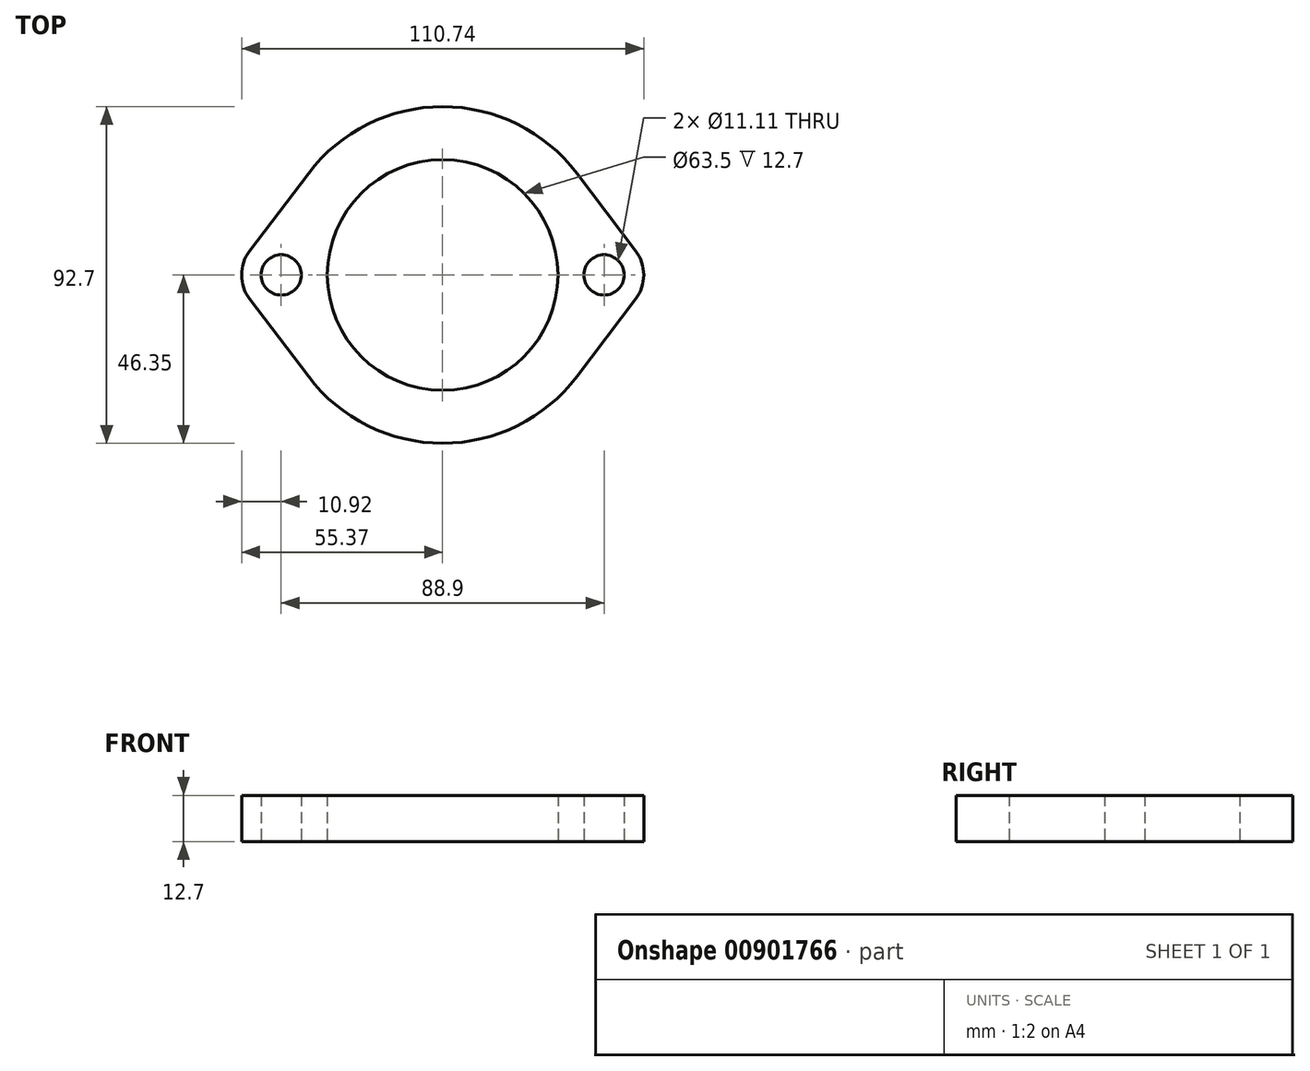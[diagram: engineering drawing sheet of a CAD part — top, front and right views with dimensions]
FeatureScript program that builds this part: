
annotation { "Feature Type Name" : "Feature", "Feature Type Description" : "" }
export const myFeature = defineFeature(function(context is Context, id is Id, definition is map)
    precondition{}
    {
        {
            var Q0;
            Q0=qCreatedBy(makeId("Top.planeOp"),FACE);
            var sketch = newSketch(context, id + "F0", { "sketchPlane" : qUnion([Q0])});
            skCircle(sketch, "E0", {"center": v(0, 0) * mm, "radius": 31.75 * mm});
            skArc(sketch, "E1", {"start": v(0, 46.35) * mm, "mid": v(-20.63, 41.51) * mm, "end": v(-36.95, 27.99) * mm});
            skCircle(sketch, "E2", {"center": v(-44.45, 0) * mm, "radius": 5.56 * mm});
            skArc(sketch, "E3", {"start": v(-53.16, 6.6) * mm, "mid": v(-54.8, 3.48) * mm, "end": v(-55.37, 0) * mm});
            skLineSegment(sketch, "E4", {"start": v(-31.75, 0) * mm, "end": v(-33.53, 0) * mm});
            skLineSegment(sketch, "E5", {"start": v(-53.16, 6.6) * mm, "end": v(-36.95, 27.99) * mm});
            skLineSegment(sketch, "E6", {"start": v(-73.33, 0) * mm, "end": v(-38.9, 0) * mm, "construction": true});
            skLineSegment(sketch, "E7", {"start": v(0, 50.51) * mm, "end": v(0, -57.19) * mm, "construction": true});
            skLineSegment(sketch, "E8.trimOffspring", {"start": v(-31.75, 0) * mm, "end": v(0, 0) * mm, "construction": true});
            skLineSegment(sketch, "E9.MirrorCS", {"start": v(-53.16, -6.6) * mm, "end": v(-36.95, -27.99) * mm});
            skArc(sketch, "E10.MirrorCS", {"start": v(-53.16, -6.6) * mm, "mid": v(-54.8, -3.48) * mm, "end": v(-55.37, 0) * mm});
            skArc(sketch, "E11.MirrorCS", {"start": v(0, -46.35) * mm, "mid": v(-20.63, -41.51) * mm, "end": v(-36.95, -27.99) * mm});
            skArc(sketch, "E12.MirrorCS", {"start": v(0, 46.35) * mm, "mid": v(20.63, 41.51) * mm, "end": v(36.95, 27.99) * mm});
            skLineSegment(sketch, "E13.MirrorCS", {"start": v(53.16, 6.6) * mm, "end": v(36.95, 27.99) * mm});
            skArc(sketch, "E14.MirrorCS", {"start": v(53.16, 6.6) * mm, "mid": v(54.8, 3.48) * mm, "end": v(55.37, 0) * mm});
            skArc(sketch, "E15.MirrorCS", {"start": v(53.16, -6.6) * mm, "mid": v(54.8, -3.48) * mm, "end": v(55.37, 0) * mm});
            skLineSegment(sketch, "E16.MirrorCS", {"start": v(53.16, -6.6) * mm, "end": v(36.95, -27.99) * mm});
            skArc(sketch, "E17.MirrorCS", {"start": v(0, -46.35) * mm, "mid": v(20.63, -41.51) * mm, "end": v(36.95, -27.99) * mm});
            skCircle(sketch, "E18.MirrorC", {"center": v(44.45, 0) * mm, "radius": 5.56 * mm});
            skSolve(sketch);
        }
        {
            var Q0;
            Q0 = qSketchRegion(id + "F0", true);
            extrude(context, id + "F1", {"entities" : qUnion([Q0]), "depth" : 12.7 * mm, "offsetDistance" : 25 * mm});
        }
    });
